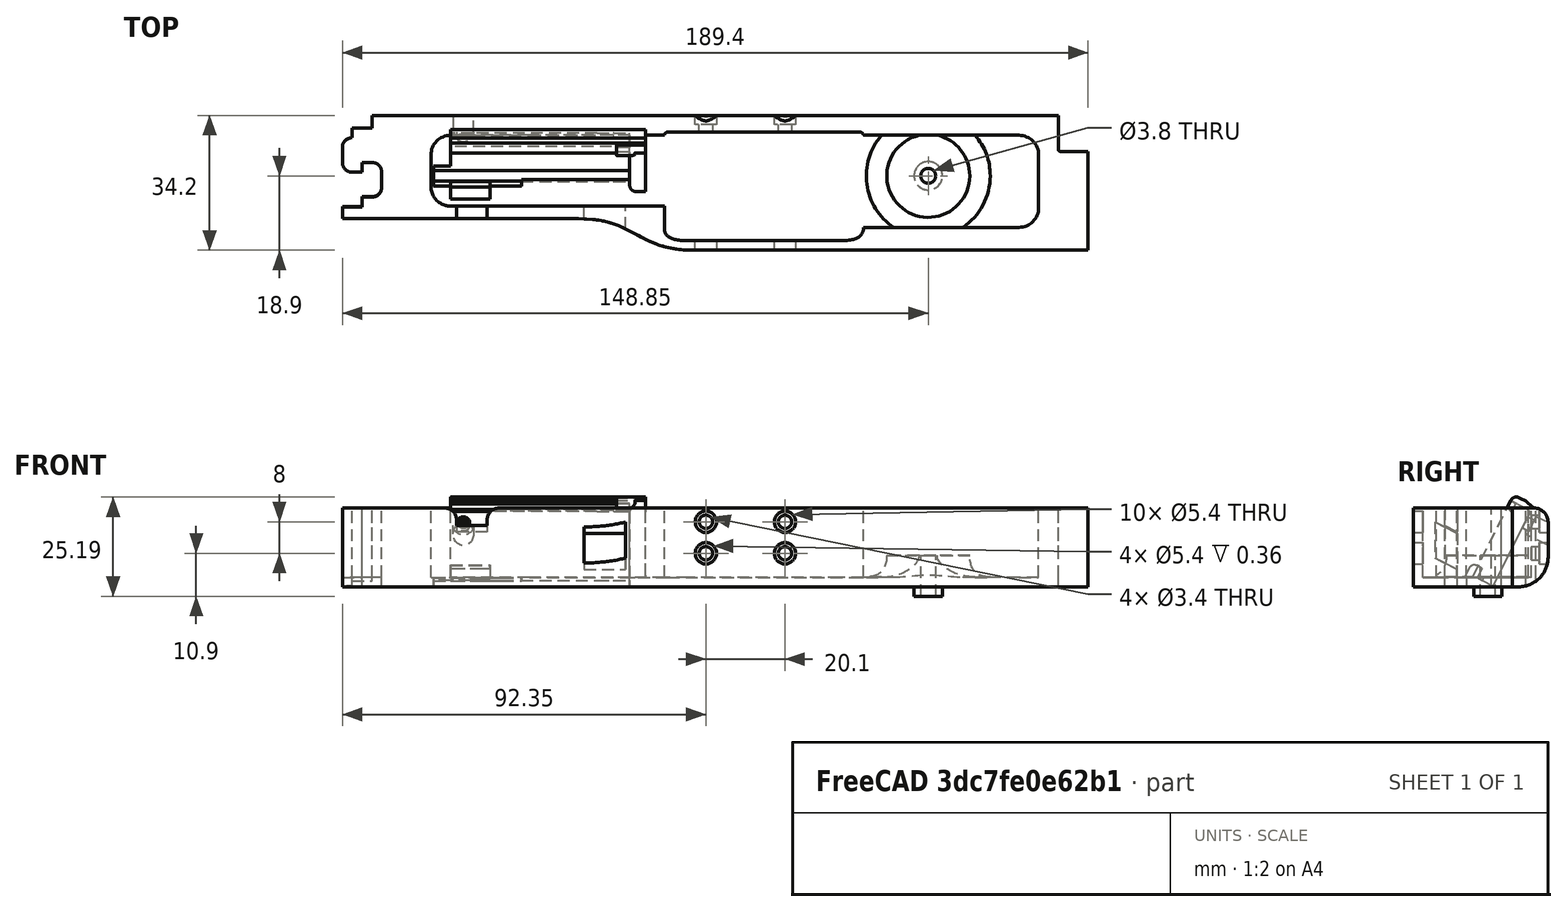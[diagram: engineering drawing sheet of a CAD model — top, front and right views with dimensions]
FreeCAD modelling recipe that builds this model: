
FCSTD DOCUMENT  (FreeCAD 0.19R0.19.2)
Label: v0_991
License: All rights reserved
LicenseURL: http://en.wikipedia.org/wiki/All_rights_reserved
objects: Sketcher::SketchObject×34, Part::Extrusion×28, Part::Cut×14, Part::Fillet×13, Part::MultiFuse×10, Part::Box×8, App::MeasureDistance×4, Part::Revolution×1, Mesh::Feature×1
note: 108 computed .brp shape members not serialized (recipe doc carries the construction recipe); baked Part::Feature solids carry a one-line shape summary decoded from their .brp

FEATURE [Sketcher::SketchObject] Sketch
  FullyConstrained = true
  sketch-geometry (36):
    g0: LineSegment StartX=0 StartY=0 StartZ=0 EndX=154.4 EndY=0 EndZ=0
    g1: LineSegment StartX=154.4 StartY=0 StartZ=0 EndX=154.4 EndY=-7.6 EndZ=0
    g2: LineSegment StartX=32.5209 StartY=-26.2 StartZ=0 EndX=-7.5 EndY=-26.2 EndZ=0
    g3-g7: Circle x5 (B-spline internal-alignment scaffolding for g8; pole/knot coordinates omitted)
    g8: BSplineCurve PolesCount=5 KnotsCount=3 Degree=3 IsPeriodic=0
    g9: GeomPoint X=61.85 Y=-33.8 Z=0
    g10: GeomPoint X=47.185 Y=-29.9 Z=0
    g11: GeomPoint X=32.5209 Y=-26.2 Z=0
    g12: Circle CenterX=121.35 CenterY=-14.3 CenterZ=0 NormalX=0 NormalY=0 NormalZ=1 AngleXU=0 Radius=3.25
    g13: LineSegment StartX=-7.5 StartY=-26.2 StartZ=0 EndX=-27.5 EndY=-26.2 EndZ=0
    g14: LineSegment StartX=-20 StartY=0 StartZ=0 EndX=0 EndY=0 EndZ=0
    g15: LineSegment StartX=-25 StartY=-3.1 StartZ=0 EndX=-20 EndY=-3.1 EndZ=0
    g16: LineSegment StartX=-25 StartY=-3.1 StartZ=0 EndX=-25 EndY=-5.6 EndZ=0
    g17: LineSegment StartX=-27.5 StartY=-8.1 StartZ=0 EndX=-27.5 EndY=-11.85 EndZ=0
    g18: ArcOfCircle CenterX=-25 CenterY=-8.1 CenterZ=0 NormalX=0 NormalY=0 NormalZ=1 AngleXU=0 Radius=2.5 StartAngle=1.5708 EndAngle=3.14159
    g19: LineSegment StartX=-25 StartY=-14.35 StartZ=0 EndX=-22.5 EndY=-14.35 EndZ=0
    g20: ArcOfCircle CenterX=-25 CenterY=-11.85 CenterZ=0 NormalX=0 NormalY=0 NormalZ=1 AngleXU=0 Radius=2.5 StartAngle=3.14159 EndAngle=4.71239
    g21: LineSegment StartX=-22.5 StartY=-14.35 StartZ=0 EndX=-22.5 EndY=-11.85 EndZ=0
    g22: LineSegment StartX=-22.5 StartY=-11.85 StartZ=0 EndX=-20 EndY=-11.85 EndZ=0
    g23: ArcOfCircle CenterX=-20 CenterY=-14.35 CenterZ=0 NormalX=0 NormalY=0 NormalZ=1 AngleXU=0 Radius=2.5 StartAngle=8e-16 EndAngle=1.5708
    g24: LineSegment StartX=-17.5 StartY=-14.35 StartZ=0 EndX=-17.5 EndY=-18.1 EndZ=0
    g25: ArcOfCircle CenterX=-20 CenterY=-18.1 CenterZ=0 NormalX=0 NormalY=0 NormalZ=1 AngleXU=0 Radius=2.5 StartAngle=4.71239 EndAngle=6.28319
    g26: LineSegment StartX=-22.5 StartY=-20.6 StartZ=0 EndX=-20 EndY=-20.6 EndZ=0
    g27: LineSegment StartX=-22.5 StartY=-20.6 StartZ=0 EndX=-22.5 EndY=-23.1 EndZ=0
    g28: LineSegment StartX=-27.5 StartY=-23.1 StartZ=0 EndX=-22.5 EndY=-23.1 EndZ=0
    g29: LineSegment StartX=-20 StartY=-3.1 StartZ=0 EndX=-20 EndY=0 EndZ=0
    g30: LineSegment StartX=-27.5 StartY=-23.1 StartZ=0 EndX=-27.5 EndY=-26.2 EndZ=0
    g31: LineSegment StartX=154.4 StartY=-7.6 StartZ=0 EndX=154.4 EndY=-8.6 EndZ=0
    g32: ArcOfCircle CenterX=154.9 CenterY=-8.6 CenterZ=0 NormalX=0 NormalY=0 NormalZ=1 AngleXU=0 Radius=0.5 StartAngle=3.14159 EndAngle=4.71239
    g33: LineSegment StartX=154.9 StartY=-9.1 StartZ=0 EndX=161.9 EndY=-9.1 EndZ=0
    g34: LineSegment StartX=161.9 StartY=-9.1 StartZ=0 EndX=161.9 EndY=-33.8 EndZ=0
    g35: LineSegment StartX=161.9 StartY=-33.8 StartZ=0 EndX=61.85 EndY=-33.8 EndZ=0
  constraints (72):
    c: PointOnObject(g0,g-2)
    c: Horizontal(g0)
    c: Distance(g0) = 154.4
    c: DistanceY(g-1,g0) = 0
    c: Vertical(g1)
    c: Distance(g1) = 7.6
    c: Coincident(g1,g0)
    c: Horizontal(g2)
    c: Block(g2)
    c: Weight(g3) = 1
    c: Coincident(g8,g2)
    c: InternalAlignment(g3-g7 -> g8) x5
    c: InternalAlignment(g9,g8)
    c: InternalAlignment(g10,g8)
    c: InternalAlignment(g11,g8)
    c: Block(g12)
    c: Coincident(g13,g2)
    c: Horizontal(g13)
    c: Distance(g13) = 20
    c: Horizontal(g14)
    c: Distance(g14) = 20
    c: Coincident(g14,g0)
    c: Horizontal(g15)
    c: Vertical(g16)
    c: Coincident(g16,g15)
    c: Vertical(g17)
    c: Coincident(g18,g16)
    c: Block(g18)
    c: Coincident(g17,g18)
    c: Horizontal(g19)
    c: Coincident(g20,g17)
    c: Block(g20)
    c: Block(g19)
    c: Vertical(g21)
    c: Coincident(g21,g19)
    c: Horizontal(g22)
    c: Coincident(g22,g21)
    c: Coincident(g23,g22)
    c: Vertical(g24)
    c: Block(g23)
    c: Coincident(g24,g23)
    c: Coincident(g25,g24)
    c: Block(g25)
    c: Horizontal(g26)
    c: Coincident(g26,g25)
    c: Vertical(g27)
    c: Coincident(g27,g26)
    c: Horizontal(g28)
    c: Coincident(g28,g27)
    c: Block(g15)
    c: Block(g28)
    c: Coincident(g29,g15)
    c: Coincident(g29,g14)
    c: Vertical(g29)
    c: Coincident(g30,g28)
    c: Coincident(g30,g13)
    c: Vertical(g30)
    c: Vertical(g31)
    c: Distance(g31) = 1
    c: Coincident(g31,g1)
    c: Coincident(g32,g31)
    c: Block(g32)
    c: Coincident(g33,g32)
    c: Horizontal(g33)
    c: Coincident(g34,g33)
    c: Vertical(g34)
    c: Block(g34)
    c: Coincident(g35,g34)
    c: Horizontal(g35)
    c: Block(g35)
    c: Coincident(g8,g35)
    c: Block(g8)
FEATURE [Part::Extrusion] Extrude  label="mainBodyBaseExtrude"
  Base = -> Sketch
  Dir = (0,0,1)
  DirMode = 2
  FaceMakerClass = Part::FaceMakerBullseye
  LengthFwd = 2.4
  LengthRev = 0
  Solid = true
  Symmetric = false
FEATURE [Sketcher::SketchObject] Sketch001
  FullyConstrained = true
  sketch-geometry (59):
    g0: ArcOfCircle CenterX=144.4 CenterY=-10 CenterZ=0 NormalX=0 NormalY=0 NormalZ=1 AngleXU=0 Radius=5 StartAngle=4.345e-13 EndAngle=1.5708
    g1: LineSegment StartX=32.5209 StartY=-26.2 StartZ=0 EndX=-7.49911 EndY=-26.2 EndZ=0
    g2: LineSegment StartX=0 StartY=0 StartZ=0 EndX=154.4 EndY=0 EndZ=0
    g3-g7: Circle x5 (B-spline internal-alignment scaffolding for g8; pole/knot coordinates omitted)
    g8: BSplineCurve PolesCount=5 KnotsCount=3 Degree=3 IsPeriodic=0
    g9: GeomPoint X=61.85 Y=-33.8 Z=0
    g10: GeomPoint X=47.1857 Y=-29.9 Z=0
    g11: GeomPoint X=32.5209 Y=-26.2 Z=0
    g12: LineSegment StartX=154.4 StartY=0 StartZ=0 EndX=154.4 EndY=-7.6 EndZ=0
    g13: LineSegment StartX=20 StartY=-5 StartZ=0 EndX=54.35 EndY=-5 EndZ=0
    g14: LineSegment StartX=104.85 StartY=-5 StartZ=0 EndX=144.4 EndY=-5 EndZ=0
    g15: LineSegment StartX=54.35 StartY=-23 StartZ=0 EndX=20 EndY=-23 EndZ=0
    g16: LineSegment StartX=-27.4991 StartY=-26.2 StartZ=0 EndX=-7.49911 EndY=-26.2 EndZ=0
    g17: LineSegment StartX=-20 StartY=0 StartZ=0 EndX=0 EndY=0 EndZ=0
    g18: LineSegment StartX=-27.4991 StartY=-23.2 StartZ=0 EndX=-22.5 EndY=-23.2 EndZ=0
    g19: LineSegment StartX=-22.5 StartY=-20.7 StartZ=0 EndX=-22.5 EndY=-23.2 EndZ=0
    g20: LineSegment StartX=-22.5 StartY=-20.7 StartZ=0 EndX=-20 EndY=-20.7 EndZ=0
    g21: ArcOfCircle CenterX=-20 CenterY=-18.2 CenterZ=0 NormalX=0 NormalY=0 NormalZ=1 AngleXU=0 Radius=2.5 StartAngle=4.71239 EndAngle=6.28319
    g22: LineSegment StartX=-17.5 StartY=-14.4 StartZ=0 EndX=-17.5 EndY=-18.2 EndZ=0
    g23: ArcOfCircle CenterX=-20 CenterY=-14.4 CenterZ=0 NormalX=0 NormalY=0 NormalZ=1 AngleXU=0 Radius=2.5 StartAngle=9e-16 EndAngle=1.5708
    g24: LineSegment StartX=-22.5 StartY=-11.9 StartZ=0 EndX=-20 EndY=-11.9 EndZ=0
    g25: LineSegment StartX=-22.5 StartY=-14.4 StartZ=0 EndX=-22.5 EndY=-11.9 EndZ=0
    g26: LineSegment StartX=-25 StartY=-14.4 StartZ=0 EndX=-22.5 EndY=-14.4 EndZ=0
    g27: ArcOfCircle CenterX=-25 CenterY=-11.9 CenterZ=0 NormalX=0 NormalY=0 NormalZ=1 AngleXU=0 Radius=2.5 StartAngle=3.14159 EndAngle=4.71239
    g28: LineSegment StartX=-27.5 StartY=-8.1 StartZ=0 EndX=-27.5 EndY=-11.9 EndZ=0
    g29: ArcOfCircle CenterX=-25 CenterY=-8.1 CenterZ=0 NormalX=0 NormalY=0 NormalZ=1 AngleXU=0 Radius=2.5 StartAngle=1.5708 EndAngle=3.14159
    g30: LineSegment StartX=-25 StartY=-3.1 StartZ=0 EndX=-25 EndY=-5.6 EndZ=0
    g31: LineSegment StartX=-20 StartY=-3.1 StartZ=0 EndX=-25 EndY=-3.1 EndZ=0
    g32: LineSegment StartX=-20 StartY=0 StartZ=0 EndX=-20 EndY=-3.1 EndZ=0
    g33: LineSegment StartX=-27.4991 StartY=-26.2 StartZ=0 EndX=-27.4991 EndY=-23.2 EndZ=0
    g34: LineSegment StartX=4.09e-14 StartY=-5 StartZ=0 EndX=20 EndY=-5 EndZ=0
    g35: ArcOfCircle CenterX=7.1e-15 CenterY=-18 CenterZ=0 NormalX=0 NormalY=0 NormalZ=1 AngleXU=0 Radius=5 StartAngle=3.14159 EndAngle=4.71239
    g36: ArcOfCircle CenterX=4.26e-14 CenterY=-10 CenterZ=0 NormalX=0 NormalY=0 NormalZ=1 AngleXU=0 Radius=5 StartAngle=1.5708 EndAngle=3.14159
    g37: LineSegment StartX=-5 StartY=-18 StartZ=0 EndX=-5 EndY=-10 EndZ=0
    g38: LineSegment StartX=6.2e-15 StartY=-23 StartZ=0 EndX=20 EndY=-23 EndZ=0
    g39: LineSegment StartX=154.4 StartY=-7.6 StartZ=0 EndX=154.4 EndY=-8.6 EndZ=0
    g40: LineSegment StartX=154.9 StartY=-9.1 StartZ=0 EndX=161.9 EndY=-9.1 EndZ=0
    g41: ArcOfCircle CenterX=154.9 CenterY=-8.6 CenterZ=0 NormalX=0 NormalY=0 NormalZ=1 AngleXU=0 Radius=0.5 StartAngle=3.14159 EndAngle=4.71299
    g42: LineSegment StartX=104.85 StartY=-28.3916 StartZ=0 EndX=144.408 EndY=-28.3916 EndZ=0
    g43: LineSegment StartX=149.4 StartY=-10 StartZ=0 EndX=149.4 EndY=-23.4 EndZ=0
    g44: ArcOfCircle CenterX=144.408 CenterY=-23.4 CenterZ=0 NormalX=0 NormalY=0 NormalZ=1 AngleXU=0 Radius=4.99164 StartAngle=4.71239 EndAngle=6.28319
    g45: LineSegment StartX=104.05 StartY=-4.2 StartZ=0 EndX=55.15 EndY=-4.2 EndZ=0
    g46: ArcOfCircle CenterX=104.05 CenterY=-5 CenterZ=0 NormalX=0 NormalY=0 NormalZ=1 AngleXU=0 Radius=0.8 StartAngle=0 EndAngle=1.5708
    g47: ArcOfCircle CenterX=55.15 CenterY=-5 CenterZ=0 NormalX=0 NormalY=0 NormalZ=1 AngleXU=0 Radius=0.8 StartAngle=1.57079 EndAngle=3.14159
    g48: BSplineCurve PolesCount=3 KnotsCount=2 Degree=2 IsPeriodic=0
    g49: GeomPoint X=54.35 Y=-28.7916 Z=0
    g50: GeomPoint X=60.35 Y=-31.7916 Z=0
    g51: BSplineCurve PolesCount=3 KnotsCount=2 Degree=2 IsPeriodic=0
    g52: GeomPoint X=98.85 Y=-31.7916 Z=0
    g53: GeomPoint X=104.85 Y=-28.7833 Z=0
    g54: LineSegment StartX=104.85 StartY=-28.3916 StartZ=0 EndX=104.85 EndY=-28.7833 EndZ=0
    g55: LineSegment StartX=54.35 StartY=-28.7916 StartZ=0 EndX=54.35 EndY=-23 EndZ=0
    g56: LineSegment StartX=60.35 StartY=-31.7916 StartZ=0 EndX=98.85 EndY=-31.7916 EndZ=0
    g57: LineSegment StartX=161.9 StartY=-33.8 StartZ=0 EndX=161.9 EndY=-9.1 EndZ=0
    g58: LineSegment StartX=61.85 StartY=-33.8 StartZ=0 EndX=161.9 EndY=-33.8 EndZ=0
  constraints (127):
    c: PointOnObject(g2,g-2)
    c: DistanceY(g-1,g2) = 0
    c: Block(g0)
    c: Horizontal(g1)
    c: Distance(g1) = 40.02
    c: Horizontal(g2)
    c: Block(g2)
    c: Weight(g3) = 1
    c: Equal(g3, g4-g7) x4
    c: Coincident(g8,g1)
    c: InternalAlignment(g3-g7 -> g8) x5
    c: InternalAlignment(g9,g8)
    c: InternalAlignment(g10,g8)
    c: InternalAlignment(g11,g8)
    c: Vertical(g12)
    c: Coincident(g12,g2)
    c: Distance(g12) = 7.6
    c: Block(g12)
    c: Horizontal(g13)
    c: Coincident(g14,g0)
    c: Horizontal(g14)
    c: Horizontal(g15)
    c: Horizontal(g16)
    c: Distance(g16) = 20
    c: Coincident(g1,g16)
    c: Horizontal(g17)
    c: Distance(g17) = 20
    c: Coincident(g17,g2)
    c: Horizontal(g31)
    c: Vertical(g30)
    c: Coincident(g29,g30)
    c: Vertical(g28)
    c: Block(g29)
    c: Coincident(g27,g28)
    c: Block(g27)
    c: Horizontal(g26)
    c: Coincident(g26,g27)
    c: Vertical(g25)
    c: Coincident(g25,g26)
    c: Horizontal(g24)
    c: Coincident(g23,g24)
    c: Block(g23)
    c: Vertical(g22)
    c: Coincident(g21,g22)
    c: Block(g21)
    c: Horizontal(g20)
    c: Coincident(g20,g21)
    c: Vertical(g19)
    c: Coincident(g19,g20)
    c: Horizontal(g18)
    c: Coincident(g18,g19)
    c: Coincident(g32,g17)
    c: Coincident(g32,g31)
    c: Vertical(g32)
    c: Coincident(g33,g16)
    c: Coincident(g33,g18)
    c: Vertical(g33)
    c: Block(g33)
    c: Block(g18)
    c: Block(g22)
    c: Block(g26)
    c: Block(g25)
    c: Block(g24)
    c: Block(g28)
    c: Block(g31)
    c: Block(g30)
    c: Horizontal(g34)
    c: Distance(g34) = 20
    c: Block(g35)
    c: Block(g36)
    c: Coincident(g37,g35)
    c: Coincident(g37,g36)
    c: Vertical(g37)
    c: Coincident(g38,g35)
    c: Coincident(g38,g15)
    c: Horizontal(g38)
    c: Block(g38)
    c: Block(g34)
    c: Block(g13)
    c: Vertical(g39)
    c: Distance(g39) = 1
    c: Coincident(g39,g12)
    c: Horizontal(g40)
    c: Coincident(g41,g39)
    c: Coincident(g41,g40)
    c: Block(g39)
    c: Block(g41)
    c: Horizontal(g42)
    c: Vertical(g43)
    c: Distance(g43) = 13.4
    c: Coincident(g43,g0)
    c: Block(g42)
    c: Block(g43)
    c: Coincident(g44,g43)
    c: Coincident(g44,g42)
    c: Block(g44)
    c: Horizontal(g45)
    c: Coincident(g46,g14)
    c: Coincident(g46,g45)
    c: Block(g46)
    c: Coincident(g47,g13)
    c: Coincident(g47,g45)
    c: Block(g47)
    c: Distance(g15) = 34.35
    c: InternalAlignment(g49,g48)
    c: InternalAlignment(g50,g48)
    c: Block(g48)
    c: InternalAlignment(g52,g51)
    c: InternalAlignment(g53,g51)
    c: Block(g51)
    c: Coincident(g54,g42)
    c: Coincident(g54,g51)
    c: Vertical(g54)
    c: Coincident(g55,g48)
    c: Coincident(g55,g15)
    c: Vertical(g55)
    c: Coincident(g56,g48)
    c: Coincident(g56,g51)
    c: Horizontal(g56)
    c: Coincident(g57,g40)
    c: Vertical(g57)
    c: Block(g57)
    c: Coincident(g58,g57)
    c: Horizontal(g58)
    c: Block(g58)
    c: Coincident(g8,g58)
    c: Block(g8)
FEATURE [Sketcher::SketchObject] Sketch005
  FullyConstrained = true
  Placement = pos=(0,0,0) rot=(1,0,0;1.5708rad)
  sketch-geometry (4):
    g0: Circle CenterX=84.95 CenterY=16.5 CenterZ=0 NormalX=0 NormalY=0 NormalZ=1 AngleXU=0 Radius=1.7
    g1: Circle CenterX=84.95 CenterY=8.5 CenterZ=0 NormalX=0 NormalY=0 NormalZ=1 AngleXU=0 Radius=1.7
    g2: Circle CenterX=64.85 CenterY=8.5 CenterZ=0 NormalX=0 NormalY=0 NormalZ=1 AngleXU=0 Radius=1.7
    g3: Circle CenterX=64.85 CenterY=16.5 CenterZ=0 NormalX=0 NormalY=0 NormalZ=1 AngleXU=0 Radius=1.7
  constraints (4):
    c: Block(g0)
    c: Block(g1)
    c: Block(g2)
    c: Block(g3)
FEATURE [Part::Extrusion] Extrude004  label="removeFromMainBodyToCreateScrewHolesForSolenoidExtrude004"
  Base = -> Sketch005
  Dir = (0,-1,1.1e-15)
  DirMode = 2
  FaceMakerClass = Part::FaceMakerBullseye
  LengthFwd = 10
  LengthRev = 0
  Solid = true
  Symmetric = false
FEATURE [Sketcher::SketchObject] Sketch004
  FullyConstrained = true
  Placement = pos=(0,0,0) rot=(1,0,0;1.5708rad)
  sketch-geometry (12):
    g0: LineSegment StartX=15.75 StartY=2.5 StartZ=0 EndX=15.75 EndY=0 EndZ=0
    g1: Circle CenterX=15.75 CenterY=2.5 CenterZ=0 NormalX=0 NormalY=0 NormalZ=1 AngleXU=0 Radius=1
    g2: Circle CenterX=10.55 CenterY=2.5 CenterZ=0 NormalX=0 NormalY=0 NormalZ=1 AngleXU=0 Radius=1
    g3: Circle CenterX=10.55 CenterY=8 CenterZ=0 NormalX=0 NormalY=0 NormalZ=1 AngleXU=0 Radius=1
    g4: BSplineCurve PolesCount=3 KnotsCount=2 Degree=2 IsPeriodic=0
    g5: GeomPoint X=15.75 Y=2.5 Z=0
    g6: GeomPoint X=10.55 Y=8 Z=0
    g7: LineSegment StartX=1.9 StartY=8 StartZ=0 EndX=10.55 EndY=8 EndZ=0
    g8: LineSegment StartX=1.9 StartY=-2.4 StartZ=0 EndX=1.9 EndY=8 EndZ=0
    g9: LineSegment StartX=3.30092 StartY=-2.4 StartZ=0 EndX=3.30092 EndY=0 EndZ=0
    g10: LineSegment StartX=15.75 StartY=0 StartZ=0 EndX=3.30092 EndY=0 EndZ=0
    g11: LineSegment StartX=3.30092 StartY=-2.4 StartZ=0 EndX=1.9 EndY=-2.4 EndZ=0
  constraints (26):
    c: Vertical(g0)
    c: Distance(g0) = 2.5
    c: Coincident(g4,g0)
    c: Weight(g1) = 1
    c: Equal(g1,g2)
    c: Equal(g1,g3)
    c: InternalAlignment(g1,g4)
    c: InternalAlignment(g2,g4)
    c: InternalAlignment(g3,g4)
    c: InternalAlignment(g5,g4)
    c: InternalAlignment(g6,g4)
    c: Block(g4)
    c: Coincident(g7,g4)
    c: Horizontal(g7)
    c: Vertical(g8)
    c: Coincident(g8,g7)
    c: Block(g8)
    c: Vertical(g9)
    c: Coincident(g10,g0)
    c: PointOnObject(g10,g-1)
    c: Horizontal(g10)
    c: Coincident(g10,g9)
    c: Block(g9)
    c: Coincident(g11,g9)
    c: Coincident(g11,g8)
    c: Horizontal(g11)
FEATURE [Sketcher::SketchObject] Sketch007
  FullyConstrained = true
  Placement = pos=(0,-14.3,2.37) rot=(-1,0,0;2.03453rad)
  sketch-geometry (6):
    g0: LineSegment StartX=0 StartY=0 StartZ=0 EndX=45.5 EndY=0 EndZ=0
    g1: LineSegment StartX=0 StartY=0 StartZ=0 EndX=0 EndY=-21.2 EndZ=0
    g2: LineSegment StartX=45.5 StartY=0 StartZ=0 EndX=49.5 EndY=0 EndZ=0
    g3: LineSegment StartX=49.5 StartY=0 StartZ=0 EndX=49.5 EndY=-21.2 EndZ=0
    g4: LineSegment StartX=49.5 StartY=-21.2 StartZ=0 EndX=0 EndY=-21.2 EndZ=0
    g5: Circle CenterX=3.25 CenterY=-18.05 CenterZ=0 NormalX=0 NormalY=0 NormalZ=1 AngleXU=0 Radius=1.6
  constraints (15):
    c: Coincident(g0,g-1)
    c: Horizontal(g0)
    c: Distance(g0) = 45.5
    c: Coincident(g1,g0)
    c: Vertical(g1)
    c: Horizontal(g2)
    c: Distance(g2) = 4
    c: Coincident(g2,g0)
    c: Coincident(g3,g2)
    c: Vertical(g3)
    c: Block(g3)
    c: Coincident(g4,g3)
    c: Horizontal(g4)
    c: Coincident(g4,g1)
    c: Block(g5)
FEATURE [Part::Extrusion] Extrude005  label="solenoidDriverHolderExtrude005"
  Base = -> Sketch007
  Dir = (0,0.894389,-0.447291)
  DirMode = 2
  FaceMakerClass = Part::FaceMakerBullseye
  LengthFwd = 10
  LengthRev = 0
  Placement = pos=(0,0,-2) rot=(0,0,1;0rad)
  Solid = true
  Symmetric = false
FEATURE [Sketcher::SketchObject] Sketch008
  FullyConstrained = false
  Placement = pos=(0,-4.3,-2.6) rot=(-1,0,0;2.03453rad)
  sketch-geometry (1):
    g0: Circle CenterX=42.25 CenterY=-3.15 CenterZ=0 NormalX=0 NormalY=0 NormalZ=1 AngleXU=0 Radius=4.5
FEATURE [Sketcher::SketchObject] Sketch009
  FullyConstrained = true
  Placement = pos=(0,-4.3,-2.6) rot=(-1,0,0;2.03453rad)
  sketch-geometry (1):
    g0: Circle CenterX=3.25 CenterY=-18.0217 CenterZ=0 NormalX=0 NormalY=0 NormalZ=1 AngleXU=0 Radius=2.6
  constraints (1):
    c: Block(g0)
FEATURE [Sketcher::SketchObject] Sketch010
  FullyConstrained = true
  Placement = pos=(0,-14.3,2.37) rot=(-1,0,0;2.03453rad)
  sketch-geometry (1):
    g0: Circle CenterX=3.25 CenterY=-18.05 CenterZ=0 NormalX=0 NormalY=0 NormalZ=1 AngleXU=0 Radius=1.6
  constraints (1):
    c: Block(g0)
FEATURE [Part::Extrusion] Extrude008  label="removeFromScrewHole3"
  Base = -> Sketch010
  Dir = (0,0.894389,-0.447291)
  DirMode = 2
  FaceMakerClass = Part::FaceMakerBullseye
  LengthFwd = -25
  LengthRev = 0
  Placement = pos=(0,4,-4) rot=(0,0,1;0rad)
  Solid = true
  Symmetric = false
FEATURE [Sketcher::SketchObject] Sketch011
  FullyConstrained = true
  Placement = pos=(0,-14.3,2.37) rot=(-1,0,0;2.03453rad)
  sketch-geometry (4):
    g0: LineSegment StartX=49.5 StartY=-21.2 StartZ=0 EndX=49.5 EndY=-22.8 EndZ=0
    g1: LineSegment StartX=49.5 StartY=-22.8 StartZ=0 EndX=0.002238 EndY=-22.8 EndZ=0
    g2: LineSegment StartX=0.002238 StartY=-21.2 StartZ=0 EndX=0.002238 EndY=-22.8 EndZ=0
    g3: LineSegment StartX=49.5 StartY=-21.2 StartZ=0 EndX=0.002238 EndY=-21.2 EndZ=0
  constraints (10):
    c: Vertical(g0)
    c: Distance(g0) = 1.6
    c: Coincident(g1,g0)
    c: Horizontal(g1)
    c: Vertical(g2)
    c: Coincident(g2,g1)
    c: Coincident(g3,g0)
    c: Coincident(g3,g2)
    c: Horizontal(g3)
    c: Block(g3)
FEATURE [Part::Extrusion] Extrude009  label="solenoidDriverTopLipFront"
  Base = -> Sketch011
  Dir = (0,0.894389,-0.447291)
  DirMode = 2
  FaceMakerClass = Part::FaceMakerBullseye
  LengthFwd = -2
  LengthRev = 0
  Placement = pos=(0,-2.9,-0.35) rot=(0,0,1;0rad)
  Solid = true
  Symmetric = false
FEATURE [Sketcher::SketchObject] Sketch012
  FullyConstrained = true
  Placement = pos=(0,-14.3,2.37) rot=(-1,0,0;2.03453rad)
  sketch-geometry (4):
    g0: LineSegment StartX=49.5 StartY=-21.2 StartZ=0 EndX=49.5 EndY=-22.8 EndZ=0
    g1: LineSegment StartX=49.5 StartY=-22.8 StartZ=0 EndX=0.002238 EndY=-22.8 EndZ=0
    g2: LineSegment StartX=0.002238 StartY=-21.2 StartZ=0 EndX=0.002238 EndY=-22.8 EndZ=0
    g3: LineSegment StartX=49.5 StartY=-21.2 StartZ=0 EndX=0.002238 EndY=-21.2 EndZ=0
  constraints (10):
    c: Vertical(g0)
    c: Distance(g0) = 1.6
    c: Coincident(g1,g0)
    c: Horizontal(g1)
    c: Vertical(g2)
    c: Coincident(g2,g1)
    c: Coincident(g3,g0)
    c: Coincident(g3,g2)
    c: Horizontal(g3)
    c: Block(g3)
FEATURE [Part::Extrusion] Extrude010  label="solenoidDriverTopLipLowerExtrude010"
  Base = -> Sketch012
  Dir = (0,0.894389,-0.447291)
  DirMode = 2
  FaceMakerClass = Part::FaceMakerBullseye
  LengthFwd = 5.05
  LengthRev = 0
  Solid = true
  Symmetric = false
FEATURE [Sketcher::SketchObject] Sketch015
  FullyConstrained = true
  Placement = pos=(0,-14.3,2.37) rot=(-1,0,0;2.03453rad)
  sketch-geometry (4):
    g0: LineSegment StartX=0 StartY=1.5 StartZ=0 EndX=0 EndY=0 EndZ=0
    g1: LineSegment StartX=0 StartY=1.5 StartZ=0 EndX=5 EndY=1.5 EndZ=0
    g2: LineSegment StartX=5 StartY=1.5 StartZ=0 EndX=5 EndY=0 EndZ=0
    g3: LineSegment StartX=0 StartY=0 StartZ=0 EndX=5 EndY=0 EndZ=0
  constraints (13):
    c: Vertical(g0)
    c: Distance(g0) = 1.5
    c: Horizontal(g1)
    c: Distance(g1) = 5
    c: Coincident(g1,g0)
    c: Vertical(g2)
    c: Distance(g2) = 1.5
    c: Coincident(g2,g1)
    c: Block(g1)
    c: Block(g2)
    c: Block(g0)
    c: Coincident(g3,g0)
    c: Coincident(g3,g2)
FEATURE [Part::Extrusion] Extrude013  label="solenoidDriverBottomLipTopExtrude012"
  Base = -> Sketch015
  Dir = (0,0.894389,-0.447291)
  DirMode = 2
  FaceMakerClass = Part::FaceMakerBullseye
  LengthFwd = -6.5
  LengthRev = 0
  Placement = pos=(0,-14.15,19.65) rot=(1,0,0;1.5708rad)
  Solid = true
  Symmetric = false
FEATURE [Sketcher::SketchObject] Sketch016
  FullyConstrained = true
  Placement = pos=(0,0,0) rot=(1,0,0;1.5708rad)
  sketch-geometry (4):
    g0: Circle CenterX=84.15 CenterY=16.5 CenterZ=0 NormalX=0 NormalY=0 NormalZ=1 AngleXU=0 Radius=2.7
    g1: Circle CenterX=64.05 CenterY=16.5 CenterZ=0 NormalX=0 NormalY=0 NormalZ=1 AngleXU=0 Radius=2.7
    g2: Circle CenterX=64.05 CenterY=8.5 CenterZ=0 NormalX=0 NormalY=0 NormalZ=1 AngleXU=0 Radius=2.7
    g3: Circle CenterX=84.15 CenterY=8.5 CenterZ=0 NormalX=0 NormalY=0 NormalZ=1 AngleXU=0 Radius=2.7
  constraints (4):
    c: Block(g0)
    c: Block(g1)
    c: Block(g3)
    c: Block(g2)
FEATURE [Part::Extrusion] Extrude014  label="removeFromMainBodyToCreateScrewHoleCounterSinks"
  Base = -> Sketch016
  Dir = (0,-1,1.1e-15)
  DirMode = 2
  FaceMakerClass = Part::FaceMakerBullseye
  LengthFwd = 1.9
  LengthRev = 0
  Placement = pos=(0.8,-0.36,0) rot=(0,0,1;0rad)
  Solid = true
  Symmetric = false
FEATURE [Part::Extrusion] Extrude015  label="removeFromScrewHole2Extrude007"
  Base = -> Sketch009
  Dir = (0,0.894389,-0.447291)
  DirMode = 2
  FaceMakerClass = Part::FaceMakerBullseye
  LengthFwd = 10
  LengthRev = 0
  Placement = pos=(0,-8,2) rot=(0,0,1;0rad)
  Solid = true
  Symmetric = false
FEATURE [Sketcher::SketchObject] Sketch017
  FullyConstrained = true
  Placement = pos=(0,-14.3,2.37) rot=(-1,0,0;2.03453rad)
  sketch-geometry (4):
    g0: LineSegment StartX=0 StartY=1.5 StartZ=0 EndX=0 EndY=0 EndZ=0
    g1: LineSegment StartX=0 StartY=1.5 StartZ=0 EndX=5 EndY=1.5 EndZ=0
    g2: LineSegment StartX=5 StartY=1.5 StartZ=0 EndX=5 EndY=0 EndZ=0
    g3: LineSegment StartX=0 StartY=0 StartZ=0 EndX=5 EndY=0 EndZ=0
  constraints (13):
    c: Vertical(g0)
    c: Distance(g0) = 1.5
    c: Horizontal(g1)
    c: Distance(g1) = 5
    c: Coincident(g1,g0)
    c: Vertical(g2)
    c: Distance(g2) = 1.5
    c: Coincident(g2,g1)
    c: Block(g1)
    c: Block(g2)
    c: Block(g0)
    c: Coincident(g3,g0)
    c: Coincident(g3,g2)
FEATURE [Part::Extrusion] Extrude016  label="solenoidDriverBottomLipTopExtrude013"
  Base = -> Sketch017
  Dir = (0,0.894389,-0.447291)
  DirMode = 2
  FaceMakerClass = Part::FaceMakerBullseye
  LengthFwd = -6.5
  LengthRev = 0
  Placement = pos=(0,-15.45,20.3) rot=(1,0,0;1.5708rad)
  Solid = true
  Symmetric = false
FEATURE [Part::Fillet] Fillet005  label="solenoidDriverBottomLipTopFillet005"
  Base = -> Extrude016
  Edges = 1 edges r=1.4: [Edge6]
FEATURE [Sketcher::SketchObject] Sketch018
  FullyConstrained = true
  Placement = pos=(38.5,-14.3,2.37) rot=(-1,0,0;2.03453rad)
  sketch-geometry (4):
    g0: LineSegment StartX=11 StartY=0 StartZ=0 EndX=11 EndY=1.5 EndZ=0
    g1: LineSegment StartX=11 StartY=0 StartZ=0 EndX=3.6 EndY=0 EndZ=0
    g2: LineSegment StartX=3.6 StartY=0 StartZ=0 EndX=3.6 EndY=1.5 EndZ=0
    g3: LineSegment StartX=11 StartY=1.5 StartZ=0 EndX=3.6 EndY=1.5 EndZ=0
  constraints (12):
    c: PointOnObject(g0,g-1)
    c: Vertical(g0)
    c: Distance(g0) = 1.5
    c: Horizontal(g1)
    c: Distance(g1) = 7.4
    c: Coincident(g1,g0)
    c: Block(g0)
    c: Coincident(g2,g1)
    c: Vertical(g2)
    c: Coincident(g3,g0)
    c: Horizontal(g3)
    c: Coincident(g2,g3)
FEATURE [Part::Extrusion] Extrude017
  Base = -> Sketch018
  Dir = (0,0.894389,-0.447291)
  DirMode = 2
  FaceMakerClass = Part::FaceMakerBullseye
  LengthFwd = 4
  LengthRev = 0
  Placement = pos=(0,-8.212,34.025) rot=(1,0,0;1.5708rad)
  Solid = true
  Symmetric = false
FEATURE [Sketcher::SketchObject] Sketch019
  FullyConstrained = true
  Placement = pos=(0,0,0) rot=(1,0,0;1.5708rad)
  sketch-geometry (4):
    g0: Circle CenterX=84.95 CenterY=8.5 CenterZ=0 NormalX=0 NormalY=0 NormalZ=1 AngleXU=0 Radius=2.7
    g1: Circle CenterX=64.85 CenterY=8.5 CenterZ=0 NormalX=0 NormalY=0 NormalZ=1 AngleXU=0 Radius=2.7
    g2: Circle CenterX=64.85 CenterY=16.5 CenterZ=0 NormalX=0 NormalY=0 NormalZ=1 AngleXU=0 Radius=2.7
    g3: Circle CenterX=84.95 CenterY=16.5 CenterZ=0 NormalX=0 NormalY=0 NormalZ=1 AngleXU=0 Radius=2.7
  constraints (4):
    c: Block(g3)
    c: Block(g2)
    c: Block(g0)
    c: Block(g1)
FEATURE [Part::Extrusion] Extrude019  label="removeSolenoidAdjusterHoles"
  Base = -> Sketch019
  Dir = (0,-1,1.1e-15)
  DirMode = 2
  FaceMakerClass = Part::FaceMakerBullseye
  LengthFwd = 6
  LengthRev = 0
  Placement = pos=(0,-30,0) rot=(0,0,1;0rad)
  Solid = true
  Symmetric = false
FEATURE [Sketcher::SketchObject] Sketch020
  FullyConstrained = true
  Placement = pos=(0,-14.3,2.37) rot=(-1,0,0;2.03453rad)
  sketch-geometry (6):
    g0: LineSegment StartX=45.5 StartY=-21.2 StartZ=0 EndX=49.5 EndY=-21.2 EndZ=0
    g1: LineSegment StartX=45.5 StartY=0 StartZ=0 EndX=49.5 EndY=0 EndZ=0
    g2: LineSegment StartX=49.5 StartY=0 StartZ=0 EndX=49.5 EndY=-21.2 EndZ=0
    g3: LineSegment StartX=4 StartY=0 StartZ=0 EndX=4 EndY=-21.2 EndZ=0
    g4: LineSegment StartX=45.5 StartY=-21.2 StartZ=0 EndX=4 EndY=-21.2 EndZ=0
    g5: LineSegment StartX=4 StartY=0 StartZ=0 EndX=45.5 EndY=0 EndZ=0
  constraints (16):
    c: Horizontal(g0)
    c: Distance(g0) = 4
    c: Horizontal(g1)
    c: Distance(g1) = 4
    c: Coincident(g2,g1)
    c: Coincident(g2,g0)
    c: Vertical(g2)
    c: Block(g2)
    c: Vertical(g3)
    c: Coincident(g4,g0)
    c: Horizontal(g4)
    c: Coincident(g4,g3)
    c: Coincident(g5,g1)
    c: Horizontal(g5)
    c: Block(g3)
    c: Block(g5)
FEATURE [Part::Box] Box  label="Cube"
  AttacherType = Attacher::AttachEngine3D
  Height = 10
  Length = 190
  Placement = pos=(-30,0,0) rot=(0,0,1;0rad)
  Width = 10
FEATURE [Part::Fillet] Fillet008
  Base = -> Box
  Edges = 1 edges r=7.5: [Edge11]
FEATURE [Part::Box] Box001  label="Cube001"
  AttacherType = Attacher::AttachEngine3D
  Height = 10
  Length = 190
  Placement = pos=(-35,0,0) rot=(0,0,1;0rad)
  Width = 10
FEATURE [Part::Cut] Cut  label="filletMain"
  Base = -> Box001
  Placement = pos=(0,-10,0) rot=(0,0,1;0rad)
  Tool = -> Fillet008
FEATURE [Part::Box] Box002  label="Cube002"
  AttacherType = Attacher::AttachEngine3D
  Height = 30
  Length = 190
  Placement = pos=(-20,0,0) rot=(0,0,1;0rad)
  Width = 10
FEATURE [Part::Box] Box003  label="Cube003"
  AttacherType = Attacher::AttachEngine3D
  Height = 10
  Length = 190
  Placement = pos=(-90,-50,-10) rot=(0,0,1;0rad)
  Width = 50
FEATURE [Sketcher::SketchObject] Sketch021
  FullyConstrained = true
  Placement = pos=(0,-14.3,2.37) rot=(-1,0,0;2.03453rad)
  sketch-geometry (6):
    g0: LineSegment StartX=41.65 StartY=-3.15 StartZ=0 EndX=38.95 EndY=-3.15 EndZ=0
    g1: LineSegment StartX=36.25 StartY=-3.15 StartZ=0 EndX=38.95 EndY=-3.15 EndZ=0
    g2: LineSegment StartX=41.65 StartY=-3.15 StartZ=0 EndX=41.65 EndY=-7.15 EndZ=0
    g3: LineSegment StartX=38.95 StartY=-7.15 StartZ=0 EndX=41.65 EndY=-7.15 EndZ=0
    g4: LineSegment StartX=38.95 StartY=-7.15 StartZ=0 EndX=36.25 EndY=-7.15 EndZ=0
    g5: LineSegment StartX=36.25 StartY=-3.15 StartZ=0 EndX=36.25 EndY=-7.15 EndZ=0
  constraints (16):
    c: Horizontal(g0)
    c: Distance(g0) = 2.7
    c: Horizontal(g1)
    c: Distance(g1) = 2.7
    c: Coincident(g1,g0)
    c: Block(g0)
    c: Coincident(g2,g0)
    c: Vertical(g2)
    c: Horizontal(g3)
    c: Coincident(g3,g2)
    c: Horizontal(g4)
    c: Coincident(g5,g1)
    c: Vertical(g5)
    c: Coincident(g5,g4)
    c: Block(g3)
    c: Block(g4)
FEATURE [Sketcher::SketchObject] Sketch022
  FullyConstrained = true
  Placement = pos=(0,-14.3,2.37) rot=(-1,0,0;2.03453rad)
  sketch-geometry (6):
    g0: LineSegment StartX=41.65 StartY=-3.15 StartZ=0 EndX=38.95 EndY=-3.15 EndZ=0
    g1: LineSegment StartX=36.25 StartY=-3.15 StartZ=0 EndX=38.95 EndY=-3.15 EndZ=0
    g2: LineSegment StartX=41.65 StartY=-3.15 StartZ=0 EndX=41.65 EndY=-7.15 EndZ=0
    g3: LineSegment StartX=38.95 StartY=-7.15 StartZ=0 EndX=41.65 EndY=-7.15 EndZ=0
    g4: LineSegment StartX=38.95 StartY=-7.15 StartZ=0 EndX=36.25 EndY=-7.15 EndZ=0
    g5: LineSegment StartX=36.25 StartY=-3.15 StartZ=0 EndX=36.25 EndY=-7.15 EndZ=0
  constraints (16):
    c: Horizontal(g0)
    c: Distance(g0) = 2.7
    c: Horizontal(g1)
    c: Distance(g1) = 2.7
    c: Coincident(g1,g0)
    c: Block(g0)
    c: Coincident(g2,g0)
    c: Vertical(g2)
    c: Horizontal(g3)
    c: Coincident(g3,g2)
    c: Horizontal(g4)
    c: Coincident(g5,g1)
    c: Vertical(g5)
    c: Coincident(g5,g4)
    c: Block(g3)
    c: Block(g4)
FEATURE [Sketcher::SketchObject] Sketch024
  FullyConstrained = true
  Placement = pos=(0,-14.3,2.37) rot=(-1,0,0;2.03453rad)
  sketch-geometry (4):
    g0: LineSegment StartX=49.5 StartY=-21.2 StartZ=0 EndX=49.5 EndY=-22.8 EndZ=0
    g1: LineSegment StartX=49.5 StartY=-22.8 StartZ=0 EndX=0.002238 EndY=-22.8 EndZ=0
    g2: LineSegment StartX=0.002238 StartY=-21.2 StartZ=0 EndX=0.002238 EndY=-22.8 EndZ=0
    g3: LineSegment StartX=49.5 StartY=-21.2 StartZ=0 EndX=0.002238 EndY=-21.2 EndZ=0
  constraints (10):
    c: Vertical(g0)
    c: Distance(g0) = 1.6
    c: Coincident(g1,g0)
    c: Horizontal(g1)
    c: Vertical(g2)
    c: Coincident(g2,g1)
    c: Coincident(g3,g0)
    c: Coincident(g3,g2)
    c: Horizontal(g3)
    c: Block(g3)
FEATURE [Sketcher::SketchObject] Sketch025
  FullyConstrained = true
  Placement = pos=(0,-14.3,2.37) rot=(-1,0,0;2.03453rad)
  sketch-geometry (4):
    g0: LineSegment StartX=0 StartY=1.5 StartZ=0 EndX=0 EndY=0 EndZ=0
    g1: LineSegment StartX=0 StartY=1.5 StartZ=0 EndX=5 EndY=1.5 EndZ=0
    g2: LineSegment StartX=5 StartY=1.5 StartZ=0 EndX=5 EndY=0 EndZ=0
    g3: LineSegment StartX=0 StartY=0 StartZ=0 EndX=5 EndY=0 EndZ=0
  constraints (13):
    c: Vertical(g0)
    c: Distance(g0) = 1.5
    c: Horizontal(g1)
    c: Distance(g1) = 5
    c: Coincident(g1,g0)
    c: Vertical(g2)
    c: Distance(g2) = 1.5
    c: Coincident(g2,g1)
    c: Block(g1)
    c: Block(g2)
    c: Block(g0)
    c: Coincident(g3,g0)
    c: Coincident(g3,g2)
FEATURE [Part::Extrusion] Extrude022  label="solenoidDriverBottomLipTopExtrude014"
  Base = -> Sketch025
  Dir = (0,0.894389,-0.447291)
  DirMode = 2
  FaceMakerClass = Part::FaceMakerBullseye
  LengthFwd = -6.5
  LengthRev = 0
  Placement = pos=(0,-15.45,20.3) rot=(1,0,0;1.5708rad)
  Solid = true
  Symmetric = false
FEATURE [Part::Fillet] Fillet013  label="solenoidDriverBottomLipTopFillet006"
  Base = -> Extrude022
  Edges = 1 edges r=1.4: [Edge6]
  Placement = pos=(5,0,0) rot=(0,0,1;0rad)
FEATURE [Sketcher::SketchObject] Sketch026
  FullyConstrained = true
  Placement = pos=(0,-14.3,2.37) rot=(-1,0,0;2.03453rad)
  sketch-geometry (4):
    g0: LineSegment StartX=0 StartY=1.5 StartZ=0 EndX=0 EndY=0 EndZ=0
    g1: LineSegment StartX=0 StartY=1.5 StartZ=0 EndX=5 EndY=1.5 EndZ=0
    g2: LineSegment StartX=5 StartY=1.5 StartZ=0 EndX=5 EndY=0 EndZ=0
    g3: LineSegment StartX=0 StartY=0 StartZ=0 EndX=5 EndY=0 EndZ=0
  constraints (13):
    c: Vertical(g0)
    c: Distance(g0) = 1.5
    c: Horizontal(g1)
    c: Distance(g1) = 5
    c: Coincident(g1,g0)
    c: Vertical(g2)
    c: Distance(g2) = 1.5
    c: Coincident(g2,g1)
    c: Block(g1)
    c: Block(g2)
    c: Block(g0)
    c: Coincident(g3,g0)
    c: Coincident(g3,g2)
FEATURE [Part::Extrusion] Extrude023  label="solenoidDriverBottomLipTopExtrude015"
  Base = -> Sketch026
  Dir = (0,0.894389,-0.447291)
  DirMode = 2
  FaceMakerClass = Part::FaceMakerBullseye
  LengthFwd = -6.5
  LengthRev = 0
  Placement = pos=(5,-14.15,19.65) rot=(1,0,0;1.5708rad)
  Solid = true
  Symmetric = false
FEATURE [Sketcher::SketchObject] Sketch027
  FullyConstrained = true
  Placement = pos=(0,-14.3,2.37) rot=(-1,0,0;2.03453rad)
  sketch-geometry (5):
    g0: LineSegment StartX=45.5 StartY=-21.2 StartZ=0 EndX=49.5 EndY=-21.2 EndZ=0
    g1: LineSegment StartX=49.5 StartY=0 StartZ=0 EndX=49.5 EndY=-21.2 EndZ=0
    g2: LineSegment StartX=49.5 StartY=0 StartZ=0 EndX=49.5 EndY=1.6 EndZ=0
    g3: LineSegment StartX=45.5 StartY=-21.2 StartZ=0 EndX=45.5 EndY=1.6 EndZ=0
    g4: LineSegment StartX=49.5 StartY=1.6 StartZ=0 EndX=45.5 EndY=1.6 EndZ=0
  constraints (14):
    c: Horizontal(g0)
    c: Distance(g0) = 4
    c: Coincident(g1,g0)
    c: Vertical(g1)
    c: Block(g1)
    c: Vertical(g2)
    c: Distance(g2) = 1.6
    c: Block(g2)
    c: Coincident(g3,g0)
    c: Vertical(g3)
    c: Coincident(g4,g2)
    c: Horizontal(g4)
    c: Block(g0)
    c: Coincident(g3,g4)
FEATURE [Part::Extrusion] Extrude024
  Base = -> Sketch027
  Dir = (0,0.894389,-0.447291)
  DirMode = 2
  FaceMakerClass = Part::FaceMakerBullseye
  LengthFwd = 6.34
  LengthRev = 0
  Placement = pos=(0,-5.59,1) rot=(0,0,1;0rad)
  Solid = true
  Symmetric = false
FEATURE [Part::Fillet] Fillet014  label="solenoidDriverSideBarFillet014"
  Base = -> Extrude024
  Edges = 1 edges r=1.4: [Edge14]
  Placement = pos=(0,0.9,-0.45) rot=(0,0,1;0rad)
FEATURE [Part::Revolution] Revolve  label="mainScrewStandRevolve"
  Angle = 360
  Axis = (0,0,1)
  Base = (0,0,0)
  FaceMakerClass = Part::FaceMakerBullseye
  Placement = pos=(121.35,-15.3,0) rot=(0,0,1;0rad)
  Solid = true
  Source = -> Sketch004
  Symmetric = false
FEATURE [Part::Extrusion] Extrude021  label="solenoidDriverTopLipLowerExtrude011"
  Base = -> Sketch024
  Dir = (0,0.894389,-0.447291)
  DirMode = 2
  FaceMakerClass = Part::FaceMakerBullseye
  LengthFwd = 5.05
  LengthRev = 0
  Solid = true
  Symmetric = false
FEATURE [Part::Fillet] Fillet012  label="solenoidDriverTopLipLowerFillet004"
  Base = -> Extrude021
  Edges = 1 edges r=1.2: [Edge7]
  Placement = pos=(0,-0.9,-1.35) rot=(0,0,1;0rad)
FEATURE [Part::Fillet] Fillet003  label="solenoidDriverTopLipLowerFillet003"
  Base = -> Extrude010
  Edges = 1 edges r=1.2: [Edge7]
  Placement = pos=(0,-3,-0.3) rot=(0,0,1;0rad)
FEATURE [Part::Extrusion] Extrude025  label="mainBodyUpperExtrude025"
  Base = -> Sketch001
  Dir = (0,0,1)
  DirMode = 2
  FaceMakerClass = Part::FaceMakerBullseye
  LengthFwd = 20
  LengthRev = 0
  Solid = true
  Symmetric = false
FEATURE [Part::MultiFuse] Fusion  label="solenoidDriverBottomLipFusion"
  Placement = pos=(0,-1.6,0) rot=(0,0,1;0rad)
  Shapes = -> [Fillet005,Fillet013,Extrude023,Extrude013]
FEATURE [Sketcher::SketchObject] Sketch028
  FullyConstrained = true
  Placement = pos=(0,-14.3,2.37) rot=(-1,0,0;2.03453rad)
  sketch-geometry (4):
    g0: LineSegment StartX=0 StartY=1.5 StartZ=0 EndX=0 EndY=0 EndZ=0
    g1: LineSegment StartX=0 StartY=1.5 StartZ=0 EndX=5 EndY=1.5 EndZ=0
    g2: LineSegment StartX=5 StartY=1.5 StartZ=0 EndX=5 EndY=0 EndZ=0
    g3: LineSegment StartX=0 StartY=0 StartZ=0 EndX=5 EndY=0 EndZ=0
  constraints (13):
    c: Vertical(g0)
    c: Distance(g0) = 1.5
    c: Horizontal(g1)
    c: Distance(g1) = 5
    c: Coincident(g1,g0)
    c: Vertical(g2)
    c: Distance(g2) = 1.5
    c: Coincident(g2,g1)
    c: Block(g1)
    c: Block(g2)
    c: Block(g0)
    c: Coincident(g3,g0)
    c: Coincident(g3,g2)
FEATURE [Part::Extrusion] Extrude026  label="solenoidDriverBottomLipTopExtrude016"
  Base = -> Sketch028
  Dir = (0,0.894389,-0.447291)
  DirMode = 2
  FaceMakerClass = Part::FaceMakerBullseye
  LengthFwd = -6.5
  LengthRev = 0
  Placement = pos=(5,-14.15,19.65) rot=(1,0,0;1.5708rad)
  Solid = true
  Symmetric = false
FEATURE [Sketcher::SketchObject] Sketch029
  FullyConstrained = true
  Placement = pos=(0,-14.3,2.37) rot=(-1,0,0;2.03453rad)
  sketch-geometry (4):
    g0: LineSegment StartX=0 StartY=1.5 StartZ=0 EndX=0 EndY=0 EndZ=0
    g1: LineSegment StartX=0 StartY=1.5 StartZ=0 EndX=5 EndY=1.5 EndZ=0
    g2: LineSegment StartX=5 StartY=1.5 StartZ=0 EndX=5 EndY=0 EndZ=0
    g3: LineSegment StartX=0 StartY=0 StartZ=0 EndX=5 EndY=0 EndZ=0
  constraints (13):
    c: Vertical(g0)
    c: Distance(g0) = 1.5
    c: Horizontal(g1)
    c: Distance(g1) = 5
    c: Coincident(g1,g0)
    c: Vertical(g2)
    c: Distance(g2) = 1.5
    c: Coincident(g2,g1)
    c: Block(g1)
    c: Block(g2)
    c: Block(g0)
    c: Coincident(g3,g0)
    c: Coincident(g3,g2)
FEATURE [Part::Extrusion] Extrude027  label="solenoidDriverBottomLipTopExtrude017"
  Base = -> Sketch029
  Dir = (0,0.894389,-0.447291)
  DirMode = 2
  FaceMakerClass = Part::FaceMakerBullseye
  LengthFwd = -6.5
  LengthRev = 0
  Placement = pos=(0,-14.15,19.65) rot=(1,0,0;1.5708rad)
  Solid = true
  Symmetric = false
FEATURE [Sketcher::SketchObject] Sketch030
  FullyConstrained = true
  Placement = pos=(0,-14.3,2.37) rot=(-1,0,0;2.03453rad)
  sketch-geometry (4):
    g0: LineSegment StartX=0 StartY=1.5 StartZ=0 EndX=0 EndY=0 EndZ=0
    g1: LineSegment StartX=0 StartY=1.5 StartZ=0 EndX=5 EndY=1.5 EndZ=0
    g2: LineSegment StartX=5 StartY=1.5 StartZ=0 EndX=5 EndY=0 EndZ=0
    g3: LineSegment StartX=0 StartY=0 StartZ=0 EndX=5 EndY=0 EndZ=0
  constraints (13):
    c: Vertical(g0)
    c: Distance(g0) = 1.5
    c: Horizontal(g1)
    c: Distance(g1) = 5
    c: Coincident(g1,g0)
    c: Vertical(g2)
    c: Distance(g2) = 1.5
    c: Coincident(g2,g1)
    c: Block(g1)
    c: Block(g2)
    c: Block(g0)
    c: Coincident(g3,g0)
    c: Coincident(g3,g2)
FEATURE [Sketcher::SketchObject] Sketch031
  FullyConstrained = true
  Placement = pos=(0,-14.3,2.37) rot=(-1,0,0;2.03453rad)
  sketch-geometry (6):
    g0: LineSegment StartX=45.5 StartY=-21.2 StartZ=0 EndX=49.5 EndY=-21.2 EndZ=0
    g1: LineSegment StartX=45.5 StartY=0 StartZ=0 EndX=49.5 EndY=0 EndZ=0
    g2: LineSegment StartX=49.5 StartY=0 StartZ=0 EndX=49.5 EndY=-21.2 EndZ=0
    g3: LineSegment StartX=4 StartY=0 StartZ=0 EndX=4 EndY=-21.2 EndZ=0
    g4: LineSegment StartX=45.5 StartY=-21.2 StartZ=0 EndX=4 EndY=-21.2 EndZ=0
    g5: LineSegment StartX=4 StartY=0 StartZ=0 EndX=45.5 EndY=0 EndZ=0
  constraints (16):
    c: Horizontal(g0)
    c: Distance(g0) = 4
    c: Horizontal(g1)
    c: Distance(g1) = 4
    c: Coincident(g2,g1)
    c: Coincident(g2,g0)
    c: Vertical(g2)
    c: Block(g2)
    c: Vertical(g3)
    c: Coincident(g4,g0)
    c: Horizontal(g4)
    c: Coincident(g4,g3)
    c: Coincident(g5,g1)
    c: Horizontal(g5)
    c: Block(g3)
    c: Block(g5)
FEATURE [Part::Extrusion] Extrude028  label="removeFromSolenoidDriverMainExtrude021"
  Base = -> Sketch031
  Dir = (0,0.894389,-0.447291)
  DirMode = 2
  FaceMakerClass = Part::FaceMakerBullseye
  LengthFwd = 3.1
  LengthRev = 0
  Placement = pos=(-4,-2.42,-0.8) rot=(0,0,1;0rad)
  Solid = true
  Symmetric = false
FEATURE [Part::Extrusion] Extrude029  label="solenoidDriverBottomLipTopExtrude018"
  Base = -> Sketch030
  Dir = (0,0.894389,-0.447291)
  DirMode = 2
  FaceMakerClass = Part::FaceMakerBullseye
  LengthFwd = -6.5
  LengthRev = 0
  Placement = pos=(5,-14.15,19.65) rot=(1,0,0;1.5708rad)
  Solid = true
  Symmetric = false
FEATURE [Sketcher::SketchObject] Sketch032
  FullyConstrained = true
  Placement = pos=(0,-14.3,2.37) rot=(-1,0,0;2.03453rad)
  sketch-geometry (4):
    g0: LineSegment StartX=0 StartY=1.5 StartZ=0 EndX=0 EndY=0 EndZ=0
    g1: LineSegment StartX=0 StartY=1.5 StartZ=0 EndX=5 EndY=1.5 EndZ=0
    g2: LineSegment StartX=5 StartY=1.5 StartZ=0 EndX=5 EndY=0 EndZ=0
    g3: LineSegment StartX=0 StartY=0 StartZ=0 EndX=5 EndY=0 EndZ=0
  constraints (13):
    c: Vertical(g0)
    c: Distance(g0) = 1.5
    c: Horizontal(g1)
    c: Distance(g1) = 5
    c: Coincident(g1,g0)
    c: Vertical(g2)
    c: Distance(g2) = 1.5
    c: Coincident(g2,g1)
    c: Block(g1)
    c: Block(g2)
    c: Block(g0)
    c: Coincident(g3,g0)
    c: Coincident(g3,g2)
FEATURE [Part::Extrusion] Extrude030  label="solenoidDriverBottomLipTopExtrude019"
  Base = -> Sketch032
  Dir = (0,0.894389,-0.447291)
  DirMode = 2
  FaceMakerClass = Part::FaceMakerBullseye
  LengthFwd = -6.5
  LengthRev = 0
  Placement = pos=(0,-14.15,19.65) rot=(1,0,0;1.5708rad)
  Solid = true
  Symmetric = false
FEATURE [Part::MultiFuse] Fusion004
  Placement = pos=(0,1.4,2.65) rot=(0,0,1;0rad)
  Shapes = -> [Extrude029,Extrude030]
FEATURE [Part::MultiFuse] Fusion003
  Placement = pos=(-2.3,0,0) rot=(0,0,1;0rad)
  Shapes = -> [Extrude028,Fusion004]
FEATURE [Sketcher::SketchObject] Sketch033
  FullyConstrained = true
  Placement = pos=(0,-14.3,2.37) rot=(-1,0,0;2.03453rad)
  sketch-geometry (4):
    g0: LineSegment StartX=0 StartY=1.5 StartZ=0 EndX=0 EndY=0 EndZ=0
    g1: LineSegment StartX=0 StartY=1.5 StartZ=0 EndX=5 EndY=1.5 EndZ=0
    g2: LineSegment StartX=5 StartY=1.5 StartZ=0 EndX=5 EndY=0 EndZ=0
    g3: LineSegment StartX=0 StartY=0 StartZ=0 EndX=5 EndY=0 EndZ=0
  constraints (13):
    c: Vertical(g0)
    c: Distance(g0) = 1.5
    c: Horizontal(g1)
    c: Distance(g1) = 5
    c: Coincident(g1,g0)
    c: Vertical(g2)
    c: Distance(g2) = 1.5
    c: Coincident(g2,g1)
    c: Block(g1)
    c: Block(g2)
    c: Block(g0)
    c: Coincident(g3,g0)
    c: Coincident(g3,g2)
FEATURE [Sketcher::SketchObject] Sketch034
  FullyConstrained = true
  Placement = pos=(0,-14.3,2.37) rot=(-1,0,0;2.03453rad)
  sketch-geometry (4):
    g0: LineSegment StartX=0 StartY=1.5 StartZ=0 EndX=0 EndY=0 EndZ=0
    g1: LineSegment StartX=0 StartY=1.5 StartZ=0 EndX=5 EndY=1.5 EndZ=0
    g2: LineSegment StartX=5 StartY=1.5 StartZ=0 EndX=5 EndY=0 EndZ=0
    g3: LineSegment StartX=0 StartY=0 StartZ=0 EndX=5 EndY=0 EndZ=0
  constraints (13):
    c: Vertical(g0)
    c: Distance(g0) = 1.5
    c: Horizontal(g1)
    c: Distance(g1) = 5
    c: Coincident(g1,g0)
    c: Vertical(g2)
    c: Distance(g2) = 1.5
    c: Coincident(g2,g1)
    c: Block(g1)
    c: Block(g2)
    c: Block(g0)
    c: Coincident(g3,g0)
    c: Coincident(g3,g2)
FEATURE [Part::Extrusion] Extrude020  label="removeFromSolenoidDriverMainExtrude020"
  Base = -> Sketch020
  Dir = (0,0.894389,-0.447291)
  DirMode = 2
  FaceMakerClass = Part::FaceMakerBullseye
  LengthFwd = 3.1
  LengthRev = 0
  Placement = pos=(-4,-2.42,-0.8) rot=(0,0,1;0rad)
  Solid = true
  Symmetric = false
FEATURE [Part::Fillet] Fillet
  Base = -> Fusion003
  Edges = 1 edges r=10: [Edge5]
  Placement = pos=(-2,0,0) rot=(0,0,1;0rad)
FEATURE [Part::MultiFuse] Fusion001
  Placement = pos=(0,1.4,2.65) rot=(0,0,1;0rad)
  Shapes = -> [Extrude026,Extrude027]
FEATURE [Part::MultiFuse] Fusion002
  Shapes = -> [Extrude020,Fusion001]
FEATURE [Sketcher::SketchObject] Sketch035
  FullyConstrained = true
  Placement = pos=(0,-14.3,2.37) rot=(-1,0,0;2.03453rad)
  sketch-geometry (4):
    g0: LineSegment StartX=0 StartY=1.5 StartZ=0 EndX=0 EndY=0 EndZ=0
    g1: LineSegment StartX=0 StartY=1.5 StartZ=0 EndX=5 EndY=1.5 EndZ=0
    g2: LineSegment StartX=5 StartY=1.5 StartZ=0 EndX=5 EndY=0 EndZ=0
    g3: LineSegment StartX=0 StartY=0 StartZ=0 EndX=5 EndY=0 EndZ=0
  constraints (13):
    c: Vertical(g0)
    c: Distance(g0) = 1.5
    c: Horizontal(g1)
    c: Distance(g1) = 5
    c: Coincident(g1,g0)
    c: Vertical(g2)
    c: Distance(g2) = 1.5
    c: Coincident(g2,g1)
    c: Block(g1)
    c: Block(g2)
    c: Block(g0)
    c: Coincident(g3,g0)
    c: Coincident(g3,g2)
FEATURE [Sketcher::SketchObject] Sketch036
  FullyConstrained = true
  Placement = pos=(0,-14.3,2.37) rot=(-1,0,0;2.03453rad)
  sketch-geometry (4):
    g0: LineSegment StartX=0 StartY=1.5 StartZ=0 EndX=0 EndY=0 EndZ=0
    g1: LineSegment StartX=0 StartY=1.5 StartZ=0 EndX=5 EndY=1.5 EndZ=0
    g2: LineSegment StartX=5 StartY=1.5 StartZ=0 EndX=5 EndY=0 EndZ=0
    g3: LineSegment StartX=0 StartY=0 StartZ=0 EndX=5 EndY=0 EndZ=0
  constraints (13):
    c: Vertical(g0)
    c: Distance(g0) = 1.5
    c: Horizontal(g1)
    c: Distance(g1) = 5
    c: Coincident(g1,g0)
    c: Vertical(g2)
    c: Distance(g2) = 1.5
    c: Coincident(g2,g1)
    c: Block(g1)
    c: Block(g2)
    c: Block(g0)
    c: Coincident(g3,g0)
    c: Coincident(g3,g2)
FEATURE [Part::Extrusion] Extrude031  label="solenoidDriverBottomLipTopExtrude020"
  Base = -> Sketch035
  Dir = (0,0.894389,-0.447291)
  DirMode = 2
  FaceMakerClass = Part::FaceMakerBullseye
  LengthFwd = -6.5
  LengthRev = 0
  Placement = pos=(5,-14.15,19.65) rot=(1,0,0;1.5708rad)
  Solid = true
  Symmetric = false
FEATURE [Part::Extrusion] Extrude032  label="solenoidDriverBottomLipTopExtrude021"
  Base = -> Sketch036
  Dir = (0,0.894389,-0.447291)
  DirMode = 2
  FaceMakerClass = Part::FaceMakerBullseye
  LengthFwd = -6.5
  LengthRev = 0
  Placement = pos=(0,-14.15,19.65) rot=(1,0,0;1.5708rad)
  Solid = true
  Symmetric = false
FEATURE [Part::MultiFuse] Fusion009
  Placement = pos=(8,1.4,2.65) rot=(0,0,1;0rad)
  Shapes = -> [Extrude031,Extrude032]
FEATURE [Part::MultiFuse] Fusion010  label="removeFromSolenoidDriver"
  Shapes = -> [Fusion009,Fillet,Fusion002]
FEATURE [Sketcher::SketchObject] Sketch037
  FullyConstrained = true
  Placement = pos=(0,0,0) rot=(1,0,0;1.5708rad)
  sketch-geometry (4):
    g0: Circle CenterX=64.05 CenterY=16.5 CenterZ=0 NormalX=0 NormalY=0 NormalZ=1 AngleXU=0 Radius=2.7
    g1: Circle CenterX=64.05 CenterY=8.5 CenterZ=0 NormalX=0 NormalY=0 NormalZ=1 AngleXU=0 Radius=2.7
    g2: Circle CenterX=84.15 CenterY=8.5 CenterZ=0 NormalX=0 NormalY=0 NormalZ=1 AngleXU=0 Radius=2.7
    g3: Circle CenterX=84.15 CenterY=16.5 CenterZ=0 NormalX=0 NormalY=0 NormalZ=1 AngleXU=0 Radius=2.7
  constraints (4):
    c: Block(g2)
    c: Block(g3)
    c: Block(g0)
    c: Block(g1)
FEATURE [Part::Extrusion] Extrude033  label="removeFromMainBodyToCreateScrewHoleCounterSinks001"
  Base = -> Sketch037
  Dir = (0,-1,1.1e-15)
  DirMode = 2
  FaceMakerClass = Part::FaceMakerBullseye
  LengthFwd = 1.9
  LengthRev = 0
  Placement = pos=(0.8,0,0) rot=(0,0,1;0rad)
  Solid = true
  Symmetric = false
FEATURE [Part::MultiFuse] Fusion011  label="removeFromMainBodyToCreateScrewHoleCounterSinks001Fusion011"
  Shapes = -> [Extrude014,Extrude033]
FEATURE [Sketcher::SketchObject] Sketch038
  FullyConstrained = true
  Placement = pos=(0,-14.3,2.37) rot=(-1,0,0;2.03453rad)
  sketch-geometry (4):
    g0: LineSegment StartX=33.9 StartY=-9.7 StartZ=0 EndX=33.9 EndY=-1.5 EndZ=0
    g1: LineSegment StartX=33.9 StartY=-1.5 StartZ=0 EndX=44.5 EndY=-1.5 EndZ=0
    g2: LineSegment StartX=33.9 StartY=-9.7 StartZ=0 EndX=44.5 EndY=-9.7 EndZ=0
    g3: LineSegment StartX=44.5 StartY=-1.5 StartZ=0 EndX=44.5 EndY=-9.7 EndZ=0
  constraints (10):
    c: Vertical(g0)
    c: Coincident(g1,g0)
    c: Horizontal(g1)
    c: Block(g1)
    c: Block(g0)
    c: Coincident(g2,g0)
    c: Horizontal(g2)
    c: Coincident(g3,g1)
    c: Coincident(g3,g2)
    c: Vertical(g3)
FEATURE [Part::Extrusion] Extrude034
  Base = -> Sketch038
  Dir = (0,0.894389,-0.447291)
  DirMode = 2
  FaceMakerClass = Part::FaceMakerBullseye
  LengthFwd = 16
  LengthRev = 0
  Placement = pos=(0,-22,7) rot=(0,0,1;0rad)
  Solid = true
  Symmetric = false
FEATURE [Sketcher::SketchObject] Sketch039
  FullyConstrained = true
  Placement = pos=(0,-14.3,2.37) rot=(-1,0,0;2.03453rad)
  sketch-geometry (4):
    g0: LineSegment StartX=5.5 StartY=-7.7 StartZ=0 EndX=13.3 EndY=-7.7 EndZ=0
    g1: LineSegment StartX=13.3 StartY=-7.7 StartZ=0 EndX=13.3 EndY=-13.1 EndZ=0
    g2: LineSegment StartX=13.3 StartY=-13.1 StartZ=0 EndX=5.5 EndY=-13.1 EndZ=0
    g3: LineSegment StartX=5.5 StartY=-7.7 StartZ=0 EndX=5.5 EndY=-13.1 EndZ=0
  constraints (12):
    c: Horizontal(g0)
    c: Distance(g0) = 7.8
    c: Coincident(g1,g0)
    c: Vertical(g1)
    c: Distance(g1) = 5.4
    c: Coincident(g2,g1)
    c: Horizontal(g2)
    c: Vertical(g3)
    c: Coincident(g3,g2)
    c: Block(g0)
    c: Block(g2)
    c: Block(g3)
FEATURE [Part::Extrusion] Extrude035  label="removeToMakeHoleForConnectorExtrude035"
  Base = -> Sketch039
  Dir = (0,0.894389,-0.447291)
  DirMode = 2
  FaceMakerClass = Part::FaceMakerBullseye
  LengthFwd = 15
  LengthRev = 0
  Placement = pos=(-4,-22,9.6469) rot=(0,0,1;0rad)
  Solid = true
  Symmetric = false
FEATURE [App::MeasureDistance] Distance  label="Distance: 4.00 mm"
  Distance = 4.00184
  P1 = (119.349,-15.3,8)
  P2 = (123.351,-15.3,8)
FEATURE [App::MeasureDistance] Distance001  label="Distance: 3.80 mm"
  Distance = 3.8
  P1 = (119.45,-15.3,8)
  P2 = (123.25,-15.3,8)
FEATURE [Part::Fillet] Fillet015
  Base = -> Extrude009
  Edges = 1 edges r=1.59: [Edge7]
FEATURE [Part::Fillet] Fillet016
  Base = -> Extrude017
  Edges = 1 edges r=1.49: [Edge12]
FEATURE [Part::Fillet] Fillet017
  Base = -> Fillet016
  Edges = 1 edges r=1.45: [Edge8]
FEATURE [Part::MultiFuse] Fusion012  label="main"
  Shapes = -> [Extrude,Revolve,Extrude005,Fillet003,Fillet012,Fillet014,Extrude025,Fusion,Fillet015,Fillet017]
FEATURE [Part::Cut] Cut001
  Base = -> Fusion012
  Tool = -> Box003
FEATURE [Part::Cut] Cut002
  Base = -> Cut001
  Tool = -> Box002
FEATURE [Part::Cut] Cut003
  Base = -> Cut002
  Tool = -> Cut
FEATURE [Part::Cut] Cut004
  Base = -> Cut003
  Tool = -> Extrude019
FEATURE [Part::Cut] Cut005
  Base = -> Cut004
  Tool = -> Fusion011
FEATURE [Part::Cut] Cut006
  Base = -> Cut005
  Tool = -> Extrude004
FEATURE [Part::Cut] Cut007
  Base = -> Cut006
  Tool = -> Extrude015
FEATURE [Part::Cut] Cut008
  Base = -> Cut007
  Tool = -> Extrude008
FEATURE [Part::Cut] Cut009
  Base = -> Cut008
  Tool = -> Fusion010
FEATURE [App::MeasureDistance] Distance002  label="Distance: 2.05 mm"
  Distance = 2.05453
  P1 = (1.5,-23.0732,21.402)
  P2 = (6e-15,-23,20)
FEATURE [Part::Cut] Cut010
  Base = -> Cut009
  Tool = -> Extrude035
FEATURE [Part::Cut] Cut011
  Base = -> Cut010
  Tool = -> Extrude034
FEATURE [Part::Fillet] Fillet018
  Base = -> Cut011
  Edges = 1 edges r=3: [Edge134]
FEATURE [Part::Fillet] Fillet019
  Base = -> Fillet018
  Edges = 1 edges r=3: [Edge29]
FEATURE [Part::Box] Box004  label="Cube004"
  AttacherType = Attacher::AttachEngine3D
  Height = 10
  Length = 200
  Placement = pos=(-30,0,0) rot=(0,0,1;0rad)
  Width = 10
FEATURE [Part::Fillet] Fillet020
  Base = -> Box004
  Edges = 1 edges r=3.6: [Edge12]
FEATURE [Part::Box] Box005  label="Cube005"
  AttacherType = Attacher::AttachEngine3D
  Height = 10
  Length = 198
  Placement = pos=(-30,0,0) rot=(0,0,1;0rad)
  Width = 10
FEATURE [Part::Cut] Cut012
  Base = -> Box005
  Tool = -> Fillet020
FEATURE [Part::Box] Box006  label="Cube006"
  AttacherType = Attacher::AttachEngine3D
  Height = 5
  Length = 200
  Placement = pos=(-30,6.4,10) rot=(1,0,0;0rad)
  Width = 5
FEATURE [Part::Box] Box007  label="Cube007"
  AttacherType = Attacher::AttachEngine3D
  Height = 5
  Length = 200
  Placement = pos=(-30,6.4,10) rot=(1,0,0;0.872665rad)
  Width = 5
FEATURE [Part::MultiFuse] Fusion013  label="removeFromMainFusion013"
  Placement = pos=(0,-10,10) rot=(0,0,1;0rad)
  Shapes = -> [Box007,Box006,Cut012]
FEATURE [Part::Cut] Cut013
  Base = -> Fillet019
  Tool = -> Fusion013
FEATURE [Mesh::Feature] v0_98_Cut013  label="v0_98-Cut013"
FEATURE [App::MeasureDistance] Distance003  label="Distance: 7.18 mm"
  Distance = 7.17719
  P1 = (117.773,-15.3145,-2.4)
  P2 = (124.951,-15.2973,-2.4)
